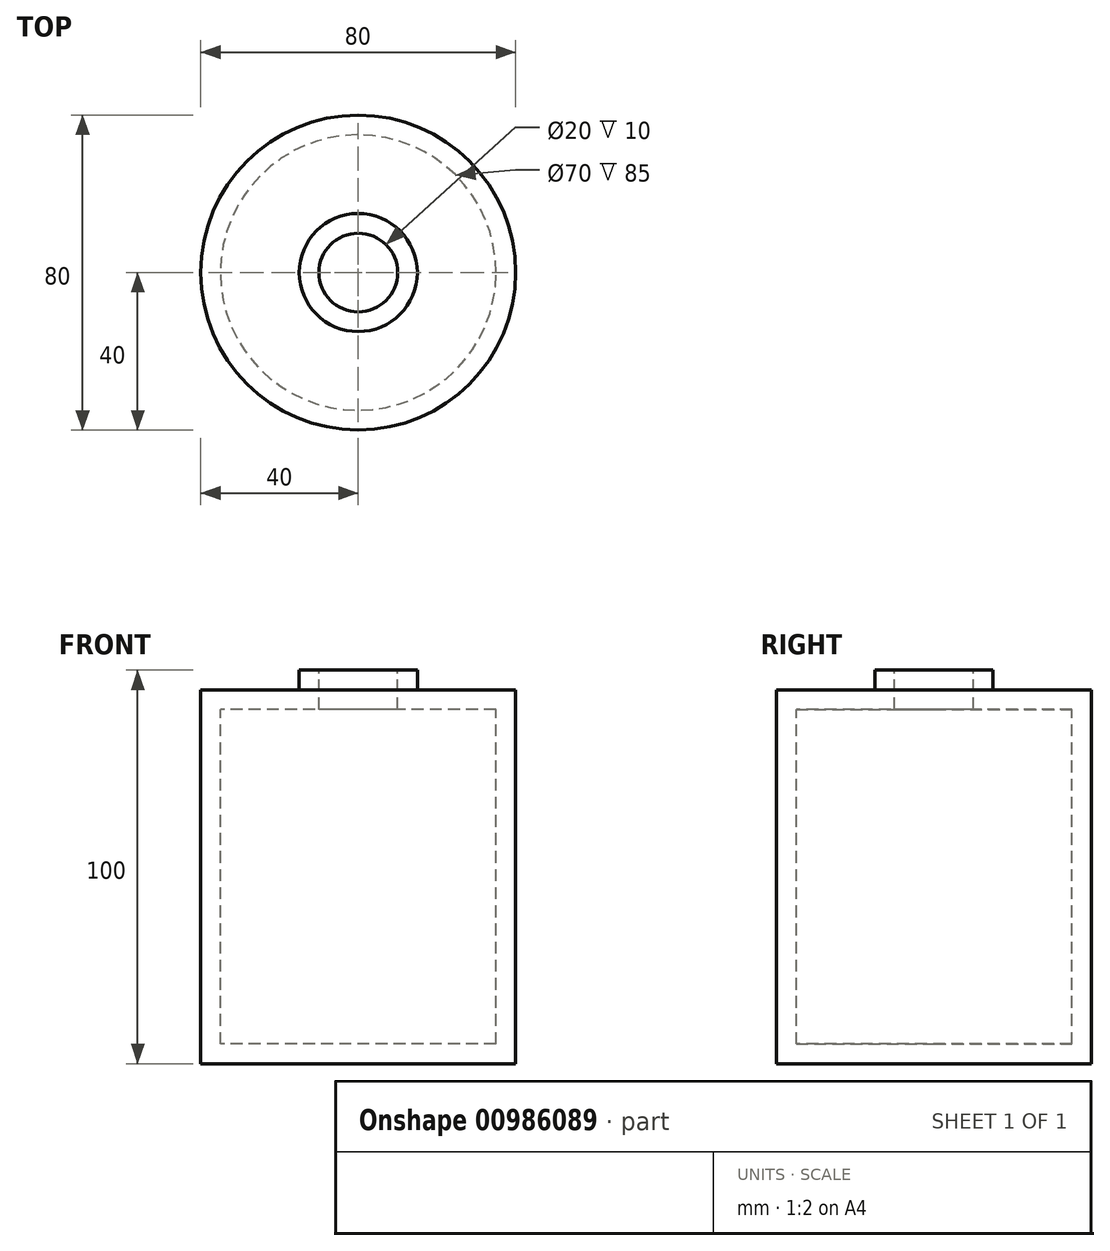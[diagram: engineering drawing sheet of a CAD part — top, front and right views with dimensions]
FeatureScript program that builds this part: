
annotation { "Feature Type Name" : "Feature", "Feature Type Description" : "" }
export const myFeature = defineFeature(function(context is Context, id is Id, definition is map)
    precondition{}
    {
        {
            var Q0;
            Q0=qCreatedBy(makeId("Front.planeOp"),FACE);
            var sketch = newSketch(context, id + "F0", { "sketchPlane" : qUnion([Q0])});
            skLineSegment(sketch, "E0", {"start": v(10, 45) * mm, "end": v(10, 35) * mm});
            skLineSegment(sketch, "E1", {"start": v(10, 35) * mm, "end": v(35, 35) * mm});
            skLineSegment(sketch, "E2", {"start": v(35, 35) * mm, "end": v(35, -50) * mm});
            skLineSegment(sketch, "E3", {"start": v(0, -50) * mm, "end": v(35, -50) * mm});
            skLineSegment(sketch, "E4.0", {"start": v(0, -55) * mm, "end": v(40, -55) * mm});
            skLineSegment(sketch, "E4.1", {"start": v(40, 40) * mm, "end": v(40, -55) * mm});
            skLineSegment(sketch, "E4.2", {"start": v(15, 40) * mm, "end": v(40, 40) * mm});
            skLineSegment(sketch, "E4.3", {"start": v(15, 45) * mm, "end": v(15, 40) * mm});
            skLineSegment(sketch, "E5", {"start": v(10, 45) * mm, "end": v(15, 45) * mm});
            skLineSegment(sketch, "E6", {"start": v(0, -50) * mm, "end": v(0, -55) * mm});
            skSolve(sketch);
        }
        {
            var Q0;
            Q0 = qSketchRegion(id + "F0", true);
            var Q1;
            Q1=sQuery(id+"F0.wireOp",EDGE,"E6");
            revolve(context, id + "F1", {"surfaceOperationType" : NewSurfaceOperationType.NEW, "entities" : qUnion([Q0]), "axis" : qUnion([Q1]), "revolveType" : RevolveType.FULL});
        }
    });
